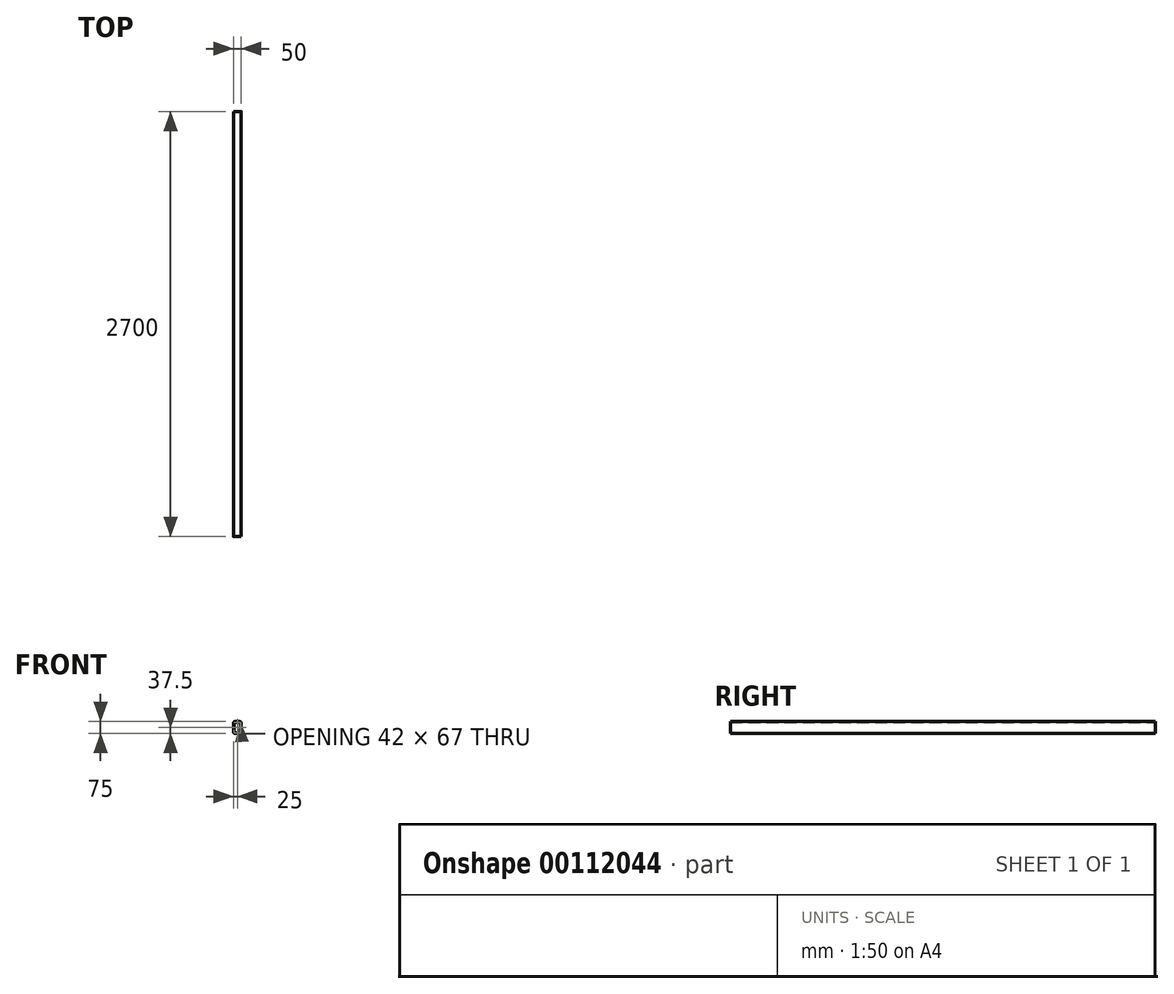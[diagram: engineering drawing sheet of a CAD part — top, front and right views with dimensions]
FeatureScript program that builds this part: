
annotation { "Feature Type Name" : "Feature", "Feature Type Description" : "" }
export const myFeature = defineFeature(function(context is Context, id is Id, definition is map)
    precondition{}
    {
        {
            var Q0;
            Q0=qCreatedBy(makeId("Front.planeOp"),FACE);
            var sketch = newSketch(context, id + "F0", { "sketchPlane" : qUnion([Q0])});
            skLineSegment(sketch, "E0.bottom", {"start": v(17, 37.5) * mm, "end": v(-17, 37.5) * mm});
            skLineSegment(sketch, "E0.top", {"start": v(17, -37.5) * mm, "end": v(-17, -37.5) * mm});
            skLineSegment(sketch, "E0.left", {"start": v(25, 29.5) * mm, "end": v(25, -29.5) * mm});
            skLineSegment(sketch, "E0.right", {"start": v(-25, 29.5) * mm, "end": v(-25, -29.5) * mm});
            skPoint(sketch, "E0.middle", {"position": v(0, 0) * mm});
            skPoint(sketch, "E1.visualSharp", {"position": v(-25, 37.5) * mm});
            skArc(sketch, "E1.filletArc", {"start": v(-17, 37.5) * mm, "mid": v(-22.66, 35.16) * mm, "end": v(-25, 29.5) * mm});
            skPoint(sketch, "E2.visualSharp", {"position": v(25, 37.5) * mm});
            skArc(sketch, "E2.filletArc", {"start": v(25, 29.5) * mm, "mid": v(22.66, 35.16) * mm, "end": v(17, 37.5) * mm});
            skPoint(sketch, "E3.visualSharp", {"position": v(-25, -37.5) * mm});
            skArc(sketch, "E3.filletArc", {"start": v(-25, -29.5) * mm, "mid": v(-22.66, -35.16) * mm, "end": v(-17, -37.5) * mm});
            skPoint(sketch, "E4.visualSharp", {"position": v(25, -37.5) * mm});
            skArc(sketch, "E4.filletArc", {"start": v(17, -37.5) * mm, "mid": v(22.66, -35.16) * mm, "end": v(25, -29.5) * mm});
            skArc(sketch, "E5.0", {"start": v(-17, 33.5) * mm, "mid": v(-19.83, 32.33) * mm, "end": v(-21, 29.5) * mm});
            skLineSegment(sketch, "E5.1", {"start": v(17, 33.5) * mm, "end": v(-17, 33.5) * mm});
            skLineSegment(sketch, "E5.2", {"start": v(-21, 29.5) * mm, "end": v(-21, -29.5) * mm});
            skArc(sketch, "E5.3", {"start": v(21, 29.5) * mm, "mid": v(19.83, 32.33) * mm, "end": v(17, 33.5) * mm});
            skArc(sketch, "E5.4", {"start": v(-21, -29.5) * mm, "mid": v(-19.83, -32.33) * mm, "end": v(-17, -33.5) * mm});
            skLineSegment(sketch, "E5.5", {"start": v(17, -33.5) * mm, "end": v(-17, -33.5) * mm});
            skArc(sketch, "E5.6", {"start": v(17, -33.5) * mm, "mid": v(19.83, -32.33) * mm, "end": v(21, -29.5) * mm});
            skLineSegment(sketch, "E5.7", {"start": v(21, 29.5) * mm, "end": v(21, -29.5) * mm});
            skSolve(sketch);
        }
        {
            var Q0;
            Q0 = qSketchRegion(id + "F0", true);
            extrude(context, id + "F1", {"entities" : qUnion([Q0]), "depth" : 2700 * mm});
        }
    });
